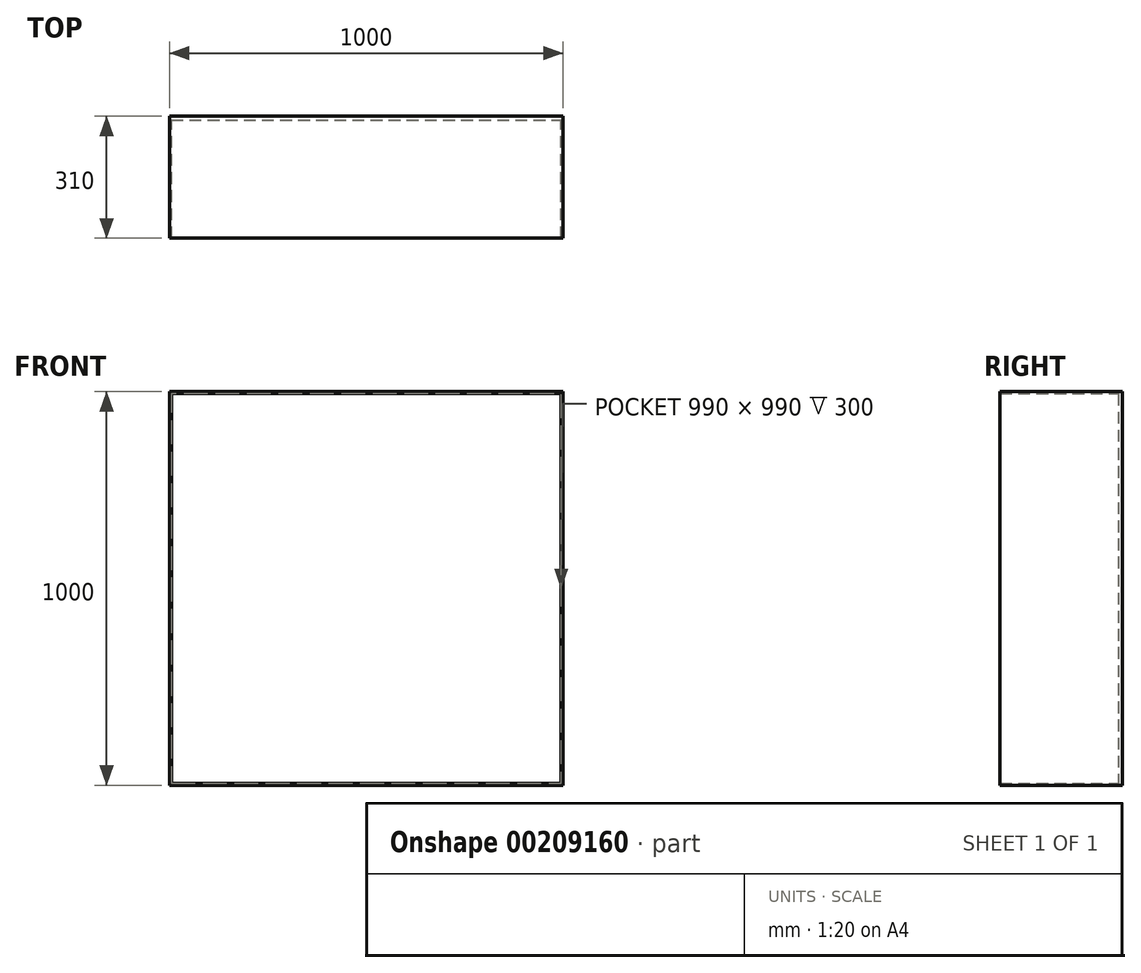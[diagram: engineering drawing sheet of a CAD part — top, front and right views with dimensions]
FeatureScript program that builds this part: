
annotation { "Feature Type Name" : "Feature", "Feature Type Description" : "" }
export const myFeature = defineFeature(function(context is Context, id is Id, definition is map)
    precondition{}
    {
        {
            var Q0;
            Q0=qCreatedBy(makeId("Front.planeOp"),FACE);
            var sketch = newSketch(context, id + "F0", { "sketchPlane" : qUnion([Q0])});
            skLineSegment(sketch, "E0.bottom", {"start": v(500, 500) * mm, "end": v(-500, 500) * mm});
            skLineSegment(sketch, "E0.top", {"start": v(500, -500) * mm, "end": v(-500, -500) * mm});
            skLineSegment(sketch, "E0.left", {"start": v(500, 500) * mm, "end": v(500, -500) * mm});
            skLineSegment(sketch, "E0.right", {"start": v(-500, 500) * mm, "end": v(-500, -500) * mm});
            skPoint(sketch, "E0.middle", {"position": v(0, 0) * mm});
            skSolve(sketch);
        }
        {
            var Q0;
            Q0 = qSketchRegion(id + "F0", true);
            extrude(context, id + "F1", {"entities" : qUnion([Q0]), "depth" : 10 * mm, "offsetDistance" : 25 * mm});
        }
        {
            var Q0;
            Q0=makeQuery(id+"F1.opExtrude","CAP_FACE",FACE,{"disambiguationData":[OSD([sQuery(id+"F0.wireOp",EDGE,"E0.bottom"),sQuery(id+"F0.wireOp",EDGE,"E0.top"),sQuery(id+"F0.wireOp",EDGE,"E0.left"),sQuery(id+"F0.wireOp",EDGE,"E0.right")])],"isStart":false});
            var sketch = newSketch(context, id + "F2", { "sketchPlane" : qUnion([Q0])});
            skLineSegment(sketch, "E1.bottom", {"start": v(-500, 500) * mm, "end": v(-495, 500) * mm});
            skLineSegment(sketch, "E1.top", {"start": v(-500, -500) * mm, "end": v(-495, -500) * mm});
            skLineSegment(sketch, "E1.left", {"start": v(-500, 500) * mm, "end": v(-500, -500) * mm});
            skLineSegment(sketch, "E1.right", {"start": v(-495, 500) * mm, "end": v(-495, -500) * mm});
            skLineSegment(sketch, "E2.bottom", {"start": v(-495, 500) * mm, "end": v(500, 500) * mm});
            skLineSegment(sketch, "E2.top", {"start": v(-495, 495) * mm, "end": v(500, 495) * mm});
            skLineSegment(sketch, "E2.left", {"start": v(-495, 500) * mm, "end": v(-495, 495) * mm});
            skLineSegment(sketch, "E2.right", {"start": v(500, 500) * mm, "end": v(500, 495) * mm});
            skLineSegment(sketch, "E3.bottom", {"start": v(500, 495) * mm, "end": v(495, 495) * mm});
            skLineSegment(sketch, "E3.top", {"start": v(500, -500) * mm, "end": v(495, -500) * mm});
            skLineSegment(sketch, "E3.left", {"start": v(500, 495) * mm, "end": v(500, -500) * mm});
            skLineSegment(sketch, "E3.right", {"start": v(495, 495) * mm, "end": v(495, -500) * mm});
            skLineSegment(sketch, "E4.bottom", {"start": v(-495, -500) * mm, "end": v(495, -500) * mm});
            skLineSegment(sketch, "E4.top", {"start": v(-495, -495) * mm, "end": v(495, -495) * mm});
            skLineSegment(sketch, "E4.left", {"start": v(-495, -500) * mm, "end": v(-495, -495) * mm});
            skLineSegment(sketch, "E4.right", {"start": v(495, -500) * mm, "end": v(495, -495) * mm});
            skSolve(sketch);
        }
        {
            var Q0;
            Q0 = qSketchRegion(id + "F2", true);
            extrude(context, id + "F3", {"entities" : qUnion([Q0]), "operationType" : NewBodyOperationType.ADD, "depth" : 300 * mm, "offsetDistance" : 25 * mm});
        }
    });
